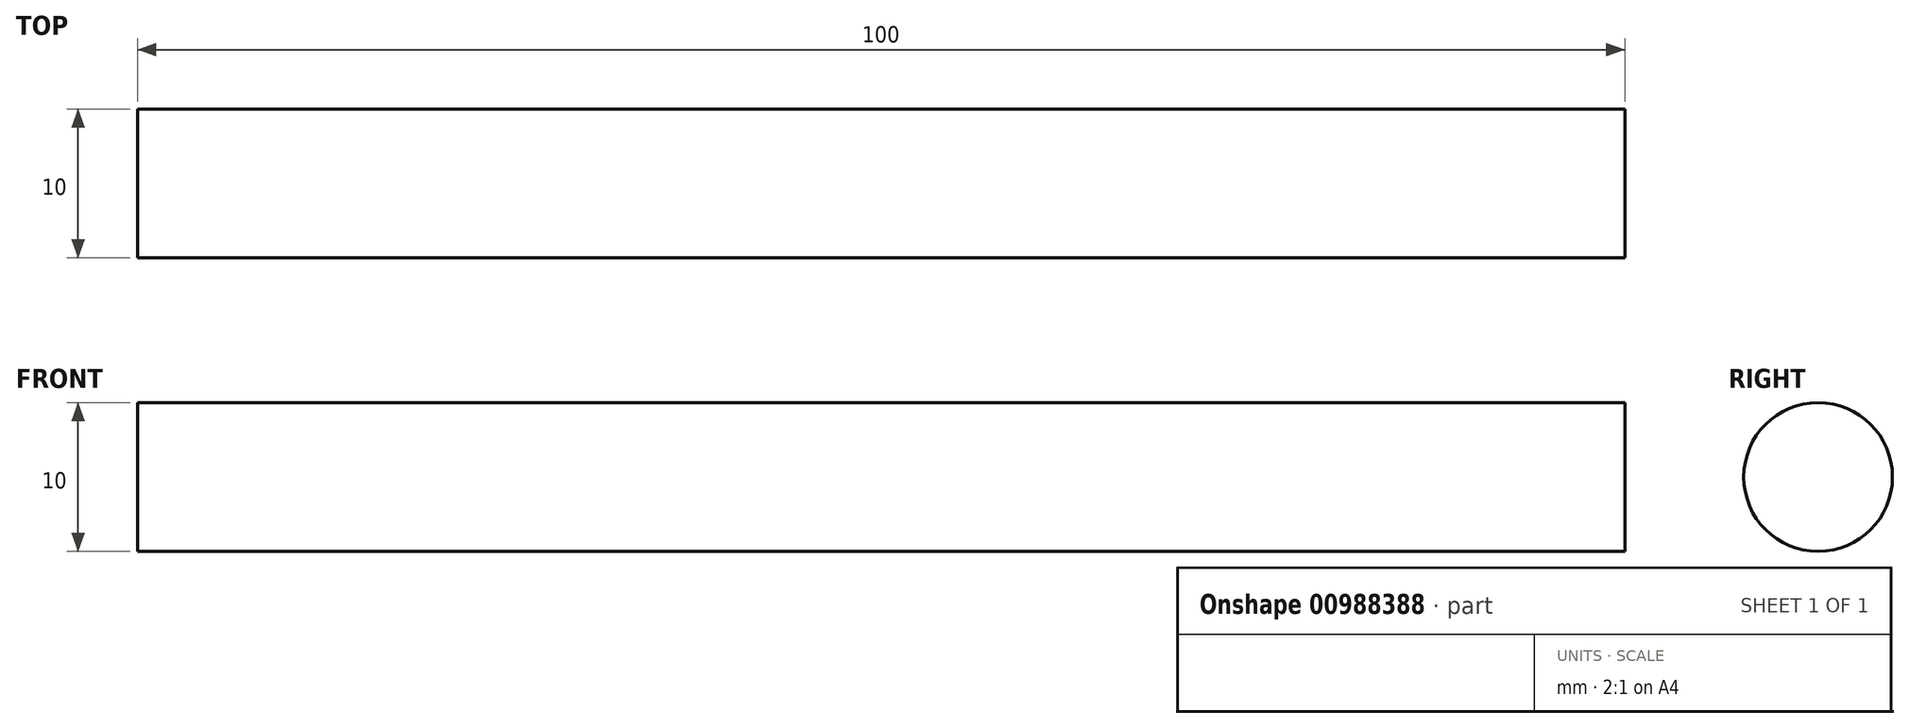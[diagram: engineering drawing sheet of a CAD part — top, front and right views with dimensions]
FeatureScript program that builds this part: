
annotation { "Feature Type Name" : "Feature", "Feature Type Description" : "" }
export const myFeature = defineFeature(function(context is Context, id is Id, definition is map)
    precondition{}
    {
        {
            var Q0;
            Q0=qCreatedBy(makeId("Right.planeOp"),FACE);
            var sketch = newSketch(context, id + "F0", { "sketchPlane" : qUnion([Q0])});
            skCircle(sketch, "E0", {"center": v(0, 0) * mm, "radius": 5 * mm});
            skSolve(sketch);
        }
        {
            var Q0;
            Q0 = qSketchRegion(id + "F0", true);
            extrude(context, id + "F1", {"entities" : qUnion([Q0]), "endBound" : BoundingType.SYMMETRIC, "depth" : 100 * mm, "offsetDistance" : 25 * mm});
        }
    });
